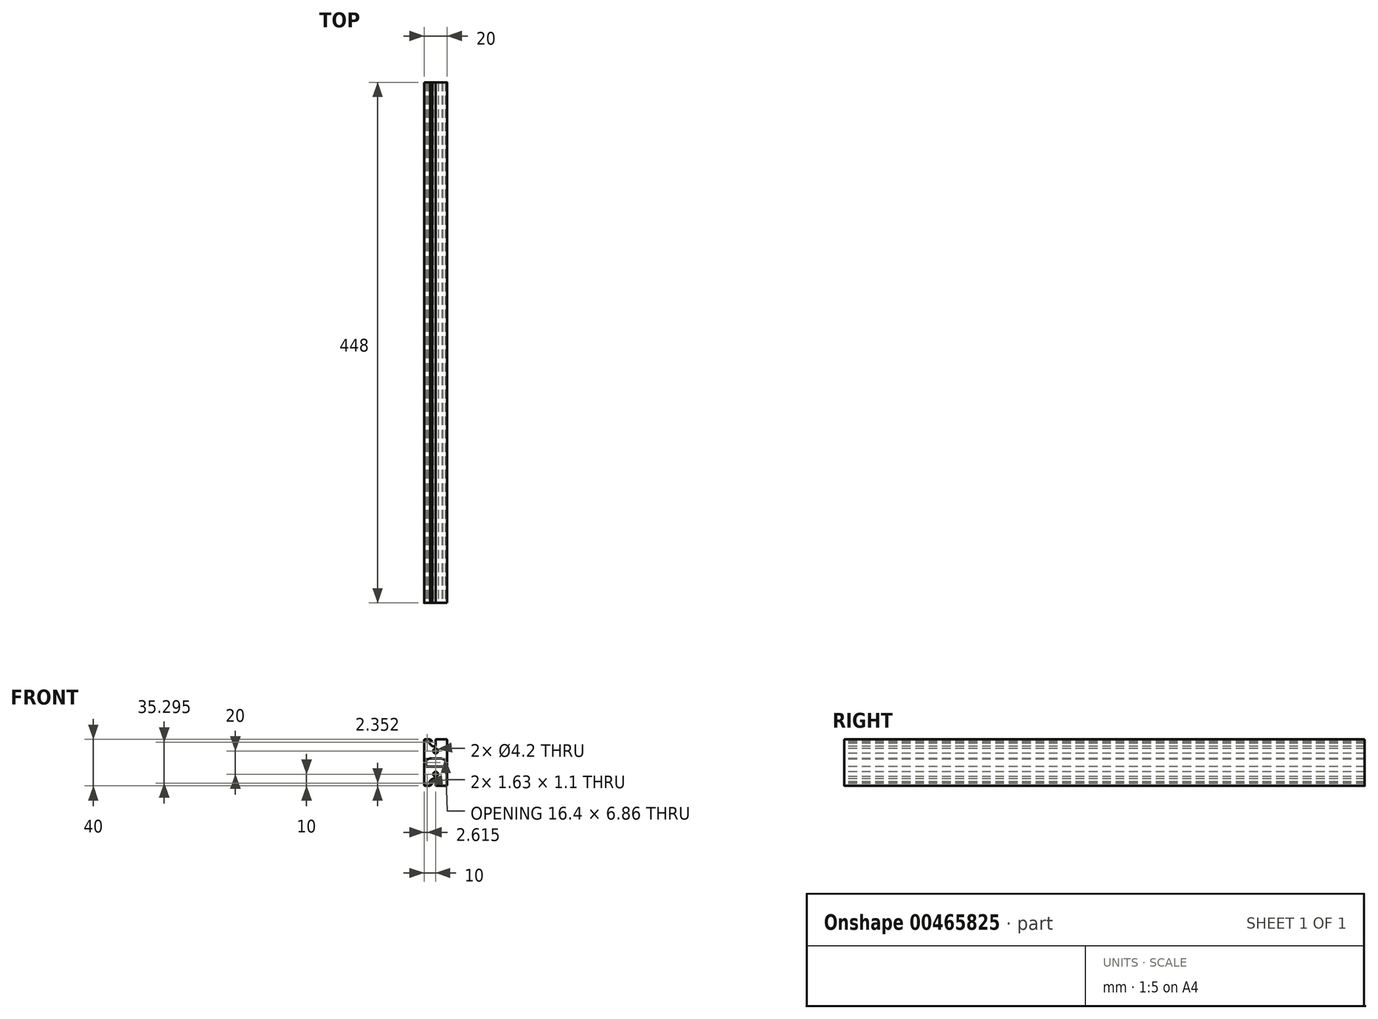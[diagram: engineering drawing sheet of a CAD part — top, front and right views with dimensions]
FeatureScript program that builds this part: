
annotation { "Feature Type Name" : "Feature", "Feature Type Description" : "" }
export const myFeature = defineFeature(function(context is Context, id is Id, definition is map)
    precondition{}
    {
        {
            var Q0;
            Q0=qCreatedBy(makeId("Front.planeOp"),FACE);
            var sketch = newSketch(context, id + "F0", { "sketchPlane" : qUnion([Q0])});
            skLineSegment(sketch, "E0.bottom", {"start": v(10, 10) * mm, "end": v(-10, 10) * mm});
            skLineSegment(sketch, "E0.top", {"start": v(10, -10) * mm, "end": v(-10, -10) * mm});
            skLineSegment(sketch, "E0.left", {"start": v(10, 10) * mm, "end": v(10, -10) * mm});
            skLineSegment(sketch, "E0.right", {"start": v(-10, 10) * mm, "end": v(-10, -10) * mm});
            skPoint(sketch, "E0.middle", {"position": v(0, 0) * mm});
            skSolve(sketch);
        }
        {
            var Q0;
            Q0=qSketchRegion(id+"F0",true);
            extrude(context, id + "F1", {"entities" : qUnion([Q0]), "depth" : 448 * mm});
        }
        {
            var Q0;
            Q0=makeQuery(id+"F1.opExtrude","CAP_FACE",FACE,{"disambiguationData":[OSD([sQuery(id+"F0.wireOp",EDGE,"E0.bottom"),sQuery(id+"F0.wireOp",EDGE,"E0.top"),sQuery(id+"F0.wireOp",EDGE,"E0.left"),sQuery(id+"F0.wireOp",EDGE,"E0.right")])],"isStart":false});
            var sketch = newSketch(context, id + "F2", { "sketchPlane" : qUnion([Q0])});
            skCircle(sketch, "E1", {"center": v(0, 0) * mm, "radius": 2.1 * mm});
            skSolve(sketch);
        }
        {
            var Q0;
            Q0=qSketchRegion(id+"F2",true);
            extrude(context, id + "F3", {"entities" : qUnion([Q0]), "operationType" : NewBodyOperationType.REMOVE, "endBound" : BoundingType.THROUGH_ALL, "oppositeDirection" : true, "depth" : 25 * mm});
        }
        {
            var Q0;
            Q0=makeQuery(id+"F1.opExtrude","SWEPT_EDGE",EDGE,{"disambiguationData":[OSD([sQuery(id+"F0.wireOp",EDGE,"E0.bottom"),sQuery(id+"F0.wireOp",EDGE,"E0.right")])]});
            var Q1;
            Q1=makeQuery(id+"F1.opExtrude","SWEPT_EDGE",EDGE,{"disambiguationData":[OSD([sQuery(id+"F0.wireOp",EDGE,"E0.bottom"),sQuery(id+"F0.wireOp",EDGE,"E0.left")])]});
            var Q2;
            Q2=makeQuery(id+"F1.opExtrude","SWEPT_EDGE",EDGE,{"disambiguationData":[OSD([sQuery(id+"F0.wireOp",EDGE,"E0.top"),sQuery(id+"F0.wireOp",EDGE,"E0.left")])]});
            var Q3;
            Q3=makeQuery(id+"F1.opExtrude","SWEPT_EDGE",EDGE,{"disambiguationData":[OSD([sQuery(id+"F0.wireOp",EDGE,"E0.top"),sQuery(id+"F0.wireOp",EDGE,"E0.right")])]});
            fillet(context, id + "F4", {"entities" : qUnion([Q0, Q1, Q2, Q3]), "radius" : 1 * mm, "tangentPropagation" : true, "allowEdgeOverflow" : false});
        }
        {
            var Q0;
            Q0=makeQuery(id+"F1.opExtrude","CAP_FACE",FACE,{"disambiguationData":[OSD([sQuery(id+"F0.wireOp",EDGE,"E0.bottom"),sQuery(id+"F0.wireOp",EDGE,"E0.top"),sQuery(id+"F0.wireOp",EDGE,"E0.left"),sQuery(id+"F0.wireOp",EDGE,"E0.right")])],"isStart":false});
            var sketch = newSketch(context, id + "F5", { "sketchPlane" : qUnion([Q0])});
            skLineSegment(sketch, "E2", {"start": v(0, 10) * mm, "end": v(-2.84, 10) * mm});
            skLineSegment(sketch, "E3", {"start": v(-2.84, 10) * mm, "end": v(-2.84, 8.2) * mm, "construction": true});
            skLineSegment(sketch, "E4", {"start": v(-2.84, 8.2) * mm, "end": v(-5.5, 8.2) * mm});
            skLineSegment(sketch, "E5", {"start": v(-2.84, 3.9) * mm, "end": v(0, 3.9) * mm});
            skLineSegment(sketch, "E6", {"start": v(0, 3.9) * mm, "end": v(0, 10) * mm});
            skLineSegment(sketch, "E7", {"start": v(-5.5, 8.2) * mm, "end": v(-5.5, 6.56) * mm});
            skLineSegment(sketch, "E8", {"start": v(-5.5, 6.56) * mm, "end": v(-2.84, 3.9) * mm});
            skPoint(sketch, "E9.endSnap0", {"position": v(-1.42, 3.9) * mm});
            skLineSegment(sketch, "E10", {"start": v(0, 0) * mm, "end": v(-9.7, 9.7) * mm, "construction": true});
            skLineSegment(sketch, "E11", {"start": v(-2.84, 8.2) * mm, "end": v(-4.64, 10) * mm});
            skLineSegment(sketch, "E12", {"start": v(-4.64, 10) * mm, "end": v(-2.84, 10) * mm});
            skLineSegment(sketch, "E13", {"start": v(-8.2, 8.2) * mm, "end": v(-6.57, 8.2) * mm});
            skLineSegment(sketch, "E14", {"start": v(-6.57, 8.2) * mm, "end": v(-6.57, 7.62) * mm});
            skLineSegment(sketch, "E15", {"start": v(-6.57, 7.62) * mm, "end": v(-7.1, 7.1) * mm});
            skLineSegment(sketch, "E16", {"start": v(-7.1, 7.1) * mm, "end": v(-8.2, 8.2) * mm});
            skSolve(sketch);
        }
        {
            var Q0;
            Q0=qSketchRegion(id+"F5",true);
            extrude(context, id + "F6", {"entities" : qUnion([Q0]), "operationType" : NewBodyOperationType.REMOVE, "endBound" : BoundingType.THROUGH_ALL, "oppositeDirection" : true, "depth" : 25 * mm});
        }
        {
            var Q0;
            Q0=qCreatedBy(makeId("Top.planeOp"),FACE);
            var sketch = newSketch(context, id + "F7", { "sketchPlane" : qUnion([Q0])});
            skLineSegment(sketch, "E17", {"start": v(0, 0) * mm, "end": v(0, -25.58) * mm, "construction": true});
            skSolve(sketch);
        }
        {
            var Q0;
            Q0=makeQuery(id+"F1.opExtrude","SWEPT_BODY",BODY,{"disambiguationData":[OSD([sQuery(id+"F0.wireOp",EDGE,"E0.bottom"),sQuery(id+"F0.wireOp",EDGE,"E0.top"),sQuery(id+"F0.wireOp",EDGE,"E0.left"),sQuery(id+"F0.wireOp",EDGE,"E0.right")])]});
            var Q1;
            {var subQ2=sQuery(id+"F0.wireOp",EDGE,"E0.top");Q1=makeQuery(id+"FZ8y8MfCgaZ2miL_1.2.F6.boolean.opBoolean","SPLIT",FACE,{"disambiguationData":[TD([makeQuery(id+"FZ8y8MfCgaZ2miL_1.2.F6.opExtrude","SWEPT_FACE",FACE,{"disambiguationData":[OSD([sQuery(id+"F5.wireOp",EDGE,"E11")])]})])],"derivedFrom":makeQuery(id+"F1.opExtrude","SWEPT_FACE",FACE,{"disambiguationData":[OSD([subQ2])]})});}
            mirror(context, id + "F8", {"operationType" : NewBodyOperationType.ADD, "entities" : qUnion([Q0]), "mirrorPlane" : qUnion([Q1])});
        }
        {
            var Q0;
            {var subQ0=makeQuery(id+"F1.opExtrude","CAP_FACE",FACE,{"disambiguationData":[OSD([sQuery(id+"F0.wireOp",EDGE,"E0.bottom"),sQuery(id+"F0.wireOp",EDGE,"E0.top"),sQuery(id+"F0.wireOp",EDGE,"E0.left"),sQuery(id+"F0.wireOp",EDGE,"E0.right")])],"isStart":false});Q0=makeQuery(id+"F8.boolean.opBoolean","MERGE",FACE,{"derivedFrom":[subQ0,makeQuery(id+"F8.opPattern","COPY",FACE,{"derivedFrom":subQ0,"instanceName":"1"})]});}
            var sketch = newSketch(context, id + "F9", { "sketchPlane" : qUnion([Q0])});
            skLineSegment(sketch, "E18.bottom", {"start": v(-8.2, -13.43) * mm, "end": v(8.2, -13.43) * mm});
            skLineSegment(sketch, "E18.top", {"start": v(-8.2, -6.57) * mm, "end": v(8.2, -6.57) * mm});
            skLineSegment(sketch, "E18.left", {"start": v(-8.2, -13.43) * mm, "end": v(-8.2, -6.57) * mm});
            skLineSegment(sketch, "E18.right", {"start": v(8.2, -13.43) * mm, "end": v(8.2, -6.57) * mm});
            skSolve(sketch);
        }
        {
            var Q0;
            Q0 = qSketchRegion(id + "F9", true);
            extrude(context, id + "F10", {"entities" : qUnion([Q0]), "operationType" : NewBodyOperationType.REMOVE, "endBound" : BoundingType.THROUGH_ALL, "oppositeDirection" : true, "depth" : 25 * mm});
        }
        {
            var Q0;
            {var subQ0=makeQuery(id+"F1.opExtrude","CAP_FACE",FACE,{"disambiguationData":[OSD([sQuery(id+"F0.wireOp",EDGE,"E0.bottom"),sQuery(id+"F0.wireOp",EDGE,"E0.top"),sQuery(id+"F0.wireOp",EDGE,"E0.left"),sQuery(id+"F0.wireOp",EDGE,"E0.right")])],"isStart":false});Q0=makeQuery(id+"F8.boolean.opBoolean","MERGE",FACE,{"derivedFrom":[subQ0,makeQuery(id+"F8.opPattern","COPY",FACE,{"derivedFrom":subQ0,"instanceName":"1"})]});}
            var sketch = newSketch(context, id + "F11", { "sketchPlane" : qUnion([Q0])});
            skArc(sketch, "E19.0", {"start": v(-10, -9) * mm, "mid": v(-9.7, -9.7) * mm, "end": v(-9, -10) * mm});
            skArc(sketch, "E19.1", {"start": v(-10, -11) * mm, "mid": v(-9.7, -10.3) * mm, "end": v(-9, -10) * mm});
            skArc(sketch, "E19.2", {"start": v(9, -10) * mm, "mid": v(9.7, -10.3) * mm, "end": v(10, -11) * mm});
            skArc(sketch, "E19.3", {"start": v(9, -10) * mm, "mid": v(9.7, -9.7) * mm, "end": v(10, -9) * mm});
            skLineSegment(sketch, "E20", {"start": v(-10, -9) * mm, "end": v(-10, -11) * mm});
            skLineSegment(sketch, "E21", {"start": v(10, -9) * mm, "end": v(10, -11) * mm});
            skLineSegment(sketch, "E22", {"start": v(8.2, -7) * mm, "end": v(5.94, -7) * mm});
            skLineSegment(sketch, "E23", {"start": v(-8.2, -7) * mm, "end": v(-5.94, -7) * mm});
            skLineSegment(sketch, "E24", {"start": v(-5.5, -6.56) * mm, "end": v(-5.94, -7) * mm});
            skLineSegment(sketch, "E25", {"start": v(5.5, -6.56) * mm, "end": v(5.94, -7) * mm});
            skLineSegment(sketch, "E26.0", {"start": v(8.2, -6.57) * mm, "end": v(5.5, -6.57) * mm});
            skLineSegment(sketch, "E27.0", {"start": v(8.2, -7) * mm, "end": v(8.2, -6.57) * mm});
            skLineSegment(sketch, "E28.0", {"start": v(-8.2, -7) * mm, "end": v(-8.2, -6.57) * mm});
            skLineSegment(sketch, "E29.0", {"start": v(-8.2, -6.57) * mm, "end": v(-5.5, -6.57) * mm});
            skPoint(sketch, "E30.orphan", {"position": v(8.2, -13.43) * mm});
            skPoint(sketch, "E31.orphan", {"position": v(-8.2, -13.43) * mm});
            skSolve(sketch);
        }
        {
            var Q0;
            Q0 = qSketchRegion(id + "F11", true);
            var Q1;
            {var subQ0=makeQuery(id+"F1.opExtrude","CAP_FACE",FACE,{"disambiguationData":[OSD([sQuery(id+"F0.wireOp",EDGE,"E0.bottom"),sQuery(id+"F0.wireOp",EDGE,"E0.top"),sQuery(id+"F0.wireOp",EDGE,"E0.left"),sQuery(id+"F0.wireOp",EDGE,"E0.right")])],"isStart":true});Q1=makeQuery(id+"F8.boolean.opBoolean","MERGE",FACE,{"derivedFrom":[subQ0,makeQuery(id+"F8.opPattern","COPY",FACE,{"derivedFrom":subQ0,"instanceName":"1"})]});}
            extrude(context, id + "F12", {"entities" : qUnion([Q0]), "operationType" : NewBodyOperationType.ADD, "endBound" : BoundingType.UP_TO_SURFACE, "oppositeDirection" : true, "endBoundEntityFace" : qUnion([Q1]), "depth" : 25 * mm});
        }
    });
